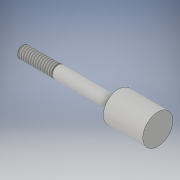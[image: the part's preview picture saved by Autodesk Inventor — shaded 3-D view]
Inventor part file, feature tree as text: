
AUTODESK INVENTOR PART (.ipt)
format: ipt  version: 2018 (Build 220112000, 112)  size: 168,960 bytes
history: native  units: in
note: dims shown in document units (in); Inventor stores cm internally (conversion verified against a paired STEP export)
features: other x70, revolve x3, sketch x3, thread x1
ambient origin geometry x8: Origin, YZ Plane, XZ Plane, XY Plane, X Axis, Y Axis, Z Axis, Center Point
bodies: Solid1 (feature_tree)
feature tree (77):
  revolve  "Revolution1"  Angle=360.0deg
  revolve  "Revolution2"  Angle=360.0deg
  thread  "Thread1"  [1 undecoded]
  revolve  "Revolution3"  [1 undecoded]
  other  "dia1_XY"
  other  "dia1_YZ"
  other  "dia1_ZX"
  other  "dia1_X"
  other  "dia1_Y"
  other  "dia1_Z"
  other  "dia1_Center"
  other  "dia12_XY"
  other  "dia12_YZ"
  other  "dia12_ZX"
  other  "dia12_X"
  other  "dia12_Y"
  other  "dia12_Z"
  other  "dia12_Center"
  other  "dia2_XY"
  other  "dia2_YZ"
  other  "dia2_ZX"
  other  "dia2_X"
  other  "dia2_Y"
  other  "dia2_Z"
  other  "dia2_Center"
  other  "dia22_XY"
  other  "dia22_YZ"
  other  "dia22_ZX"
  other  "dia22_X"
  other  "dia22_Y"
  other  "dia22_Z"
  other  "dia22_Center"
  other  "rl1_XY"
  other  "rl1_YZ"
  other  "rl1_ZX"
  other  "rl1_X"
  other  "rl1_Y"
  other  "rl1_Z"
  other  "rl1_Center"
  other  "rl2_XY"
  other  "rl2_YZ"
  other  "rl2_ZX"
  other  "rl2_X"
  other  "rl2_Y"
  other  "rl2_Z"
  other  "rl2_Center"
  other  "rod_cp_XY"
  other  "rod_cp_YZ"
  other  "rod_cp_ZX"
  other  "rod_cp_X"
  other  "rod_cp_Y"
  other  "rod_cp_Z"
  other  "rod_cp_Center"
  other  "thd1_XY"
  other  "thd1_YZ"
  other  "thd1_ZX"
  other  "thd1_X"
  other  "thd1_Y"
  other  "thd1_Z"
  other  "thd1_Center"
  other  "thd2_XY"
  other  "thd2_YZ"
  other  "thd2_ZX"
  other  "thd2_X"
  other  "thd2_Y"
  other  "thd2_Z"
  other  "thd2_Center"
  other  "to_rod_clevis_XY"
  other  "to_rod_clevis_YZ"
  other  "to_rod_clevis_ZX"
  other  "to_rod_clevis_X"
  other  "to_rod_clevis_Y"
  other  "to_rod_clevis_Z"
  other  "to_rod_clevis_Center"
  sketch  "Sketch_1"  dims[d0=360.0deg d1=360.0deg]
  sketch  "Sketch_2"  dims[d2=0.3651in d3=0.0in d4=360.0deg]
  sketch  "Sketch_30"  dims[d5=0.0in d6=0.0in d7=0.0in d8=0.0in d9=0.0in d10=0.0in]
note: 2 required parameter values undecoded (feature->parameter linkage not recoverable at this tier; creation-order binding heuristic only, values carry confidence <= 0.55)
